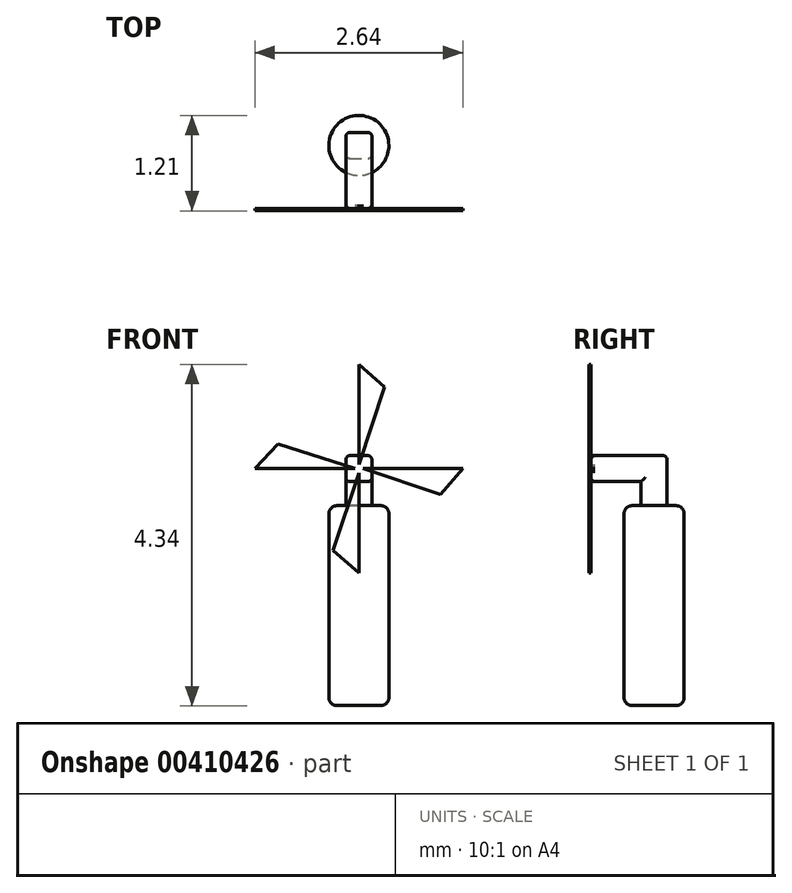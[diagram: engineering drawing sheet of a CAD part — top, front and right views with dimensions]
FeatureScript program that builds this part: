
annotation { "Feature Type Name" : "Feature", "Feature Type Description" : "" }
export const myFeature = defineFeature(function(context is Context, id is Id, definition is map)
    precondition{}
    {
        {
            var Q0;
            Q0=qCreatedBy(makeId("Front.planeOp"),FACE);
            var sketch = newSketch(context, id + "F0", { "sketchPlane" : qUnion([Q0])});
            skLineSegment(sketch, "E0.bottom", {"start": v(0, 1.24) * mm, "end": v(0.38, 1.24) * mm});
            skLineSegment(sketch, "E0.top", {"start": v(0, -1.3) * mm, "end": v(0.38, -1.3) * mm});
            skLineSegment(sketch, "E0.left", {"start": v(0, 1.24) * mm, "end": v(0, -1.3) * mm});
            skLineSegment(sketch, "E0.right", {"start": v(0.38, 1.24) * mm, "end": v(0.38, -1.3) * mm});
            skSolve(sketch);
        }
        {
            var Q0;
            Q0=makeQuery(id+"F0.imprint","IMPRINT",FACE,{"disambiguationData":[TD([[makeQuery(id+"F0.imprint","IMPRINT",EDGE,{"derivedFrom":sQuery(id+"F0.wireOp",EDGE,"E0.bottom")}),-1.0]])]});
            var Q1;
            Q1=sQuery(id+"F0.wireOp",EDGE,"E0.left");
            revolve(context, id + "F1", {"entities" : qUnion([Q0]), "axis" : qUnion([Q1]), "revolveType" : RevolveType.FULL});
        }
        {
            var Q0;
            Q0=makeQuery(id+"F1.opRevolve","SWEPT_FACE",FACE,{"disambiguationData":[OSD([sQuery(id+"F0.wireOp",EDGE,"E0.bottom")])]});
            var sketch = newSketch(context, id + "F2", { "sketchPlane" : qUnion([Q0])});
            skLineSegment(sketch, "E1.bottom", {"start": v(-0.17, 0.17) * mm, "end": v(0.17, 0.17) * mm});
            skLineSegment(sketch, "E1.top", {"start": v(-0.17, -0.17) * mm, "end": v(0.17, -0.17) * mm});
            skLineSegment(sketch, "E1.left", {"start": v(-0.17, 0.17) * mm, "end": v(-0.17, -0.17) * mm});
            skLineSegment(sketch, "E1.right", {"start": v(0.17, 0.17) * mm, "end": v(0.17, -0.17) * mm});
            skPoint(sketch, "E1.middle", {"position": v(0, 0) * mm});
            skSolve(sketch);
        }
        {
            var Q0;
            Q0 = qSketchRegion(id + "F2", true);
            extrude(context, id + "F3", {"entities" : qUnion([Q0]), "operationType" : NewBodyOperationType.ADD, "depth" : 0.64 * mm});
        }
        {
            var Q0;
            Q0=makeQuery(id+"F3.opExtrude","SWEPT_FACE",FACE,{"disambiguationData":[OSD([sQuery(id+"F2.wireOp",EDGE,"E1.top")])]});
            var sketch = newSketch(context, id + "F4", { "sketchPlane" : qUnion([Q0])});
            skLineSegment(sketch, "E2.bottom", {"start": v(-0.17, 1.88) * mm, "end": v(0.17, 1.88) * mm});
            skLineSegment(sketch, "E2.top", {"start": v(-0.17, 1.55) * mm, "end": v(0.17, 1.55) * mm});
            skLineSegment(sketch, "E2.left", {"start": v(-0.17, 1.88) * mm, "end": v(-0.17, 1.55) * mm});
            skLineSegment(sketch, "E2.right", {"start": v(0.17, 1.88) * mm, "end": v(0.17, 1.55) * mm});
            skSolve(sketch);
        }
        {
            var Q0;
            Q0 = qSketchRegion(id + "F4", true);
            extrude(context, id + "F5", {"entities" : qUnion([Q0]), "operationType" : NewBodyOperationType.ADD, "depth" : 0.64 * mm});
        }
        {
            var Q0;
            Q0 = qSketchRegion(id + "F2", true);
            extrude(context, id + "F6", {"entities" : qUnion([Q0]), "operationType" : NewBodyOperationType.ADD, "depth" : 0.64 * mm});
        }
        {
            var Q0;
            Q0=makeQuery(id+"F5.opExtrude","CAP_FACE",FACE,{"disambiguationData":[OSD([sQuery(id+"F4.wireOp",EDGE,"E2.bottom"),sQuery(id+"F4.wireOp",EDGE,"E2.top"),sQuery(id+"F4.wireOp",EDGE,"E2.left"),sQuery(id+"F4.wireOp",EDGE,"E2.right")])],"isStart":false});
            var sketch = newSketch(context, id + "F7", { "sketchPlane" : qUnion([Q0])});
            skPoint(sketch, "E3.startSnap0", {"position": v(-0.17, 1.71) * mm});
            skPoint(sketch, "E3.startSnap1", {"position": v(0, 1.55) * mm});
            skPoint(sketch, "E3.endSnap0", {"position": v(0, 1.88) * mm});
            skPoint(sketch, "E4", {"position": v(0, 1.71) * mm});
            skLineSegment(sketch, "E5", {"start": v(0, 1.77) * mm, "end": v(0, 3.04) * mm});
            skLineSegment(sketch, "E6", {"start": v(0, 3.04) * mm, "end": v(0.33, 2.75) * mm});
            skLineSegment(sketch, "E7", {"start": v(0.33, 2.75) * mm, "end": v(0, 1.77) * mm});
            skSolve(sketch);
        }
        {
            var Q0;
            {var subQ0=sQuery(id+"F7.wireOp",EDGE,"6g4KuSDk-Yey7-5Irt-Qodg-rzQO38CruASS");Q0=makeQuery(id+"F7.imprint","IMPRINT",FACE,{"disambiguationData":[TD([[makeQuery(id+"F7.imprint","IMPRINT",EDGE,{"derivedFrom":subQ0}),-1.0]])]});}
            var Q1;
            {var subQ0=sQuery(id+"F7.wireOp",EDGE,"E6");Q1=makeQuery(id+"F7.imprint","IMPRINT",FACE,{"disambiguationData":[TD([[makeQuery(id+"F7.imprint","IMPRINT",EDGE,{"derivedFrom":subQ0}),-1.0]])]});}
            var Q2;
            {var subQ0=sQuery(id+"F7.wireOp",EDGE,"E7");var subQ1=sQuery(id+"F7.wireOp",EDGE,"E5");var subQ2=makeQuery(id+"F7.imprint","INTERSECT",VERTEX,{"derivedFrom":[subQ1,subQ0]});Q2=makeQuery(id+"F7.imprint","IMPRINT",FACE,{"disambiguationData":[TD([[makeQuery(id+"F7.imprint","IMPRINT",EDGE,{"disambiguationData":[TD([[subQ2,-1.0]])],"derivedFrom":subQ1}),-1.0]])]});}
            extrude(context, id + "F8", {"entities" : qUnion([Q0, Q1, Q2]), "operationType" : NewBodyOperationType.ADD, "depth" : 0.03 * mm});
        }
        {
            var Q0;
            Q0 = qSketchRegion(id + "F7", true);
            extrude(context, id + "F9", {"entities" : qUnion([Q0]), "operationType" : NewBodyOperationType.ADD, "depth" : 0.03 * mm});
        }
        {
            var Q0;
            Q0=makeQuery(id+"F7.imprint","IMPRINT",FACE,{"disambiguationData":[TD([[makeQuery(id+"F7.imprint","IMPRINT",EDGE,{"derivedFrom":makeQuery(id+"F5.opExtrude","CAP_EDGE",EDGE,{"disambiguationData":[OSD([sQuery(id+"F4.wireOp",EDGE,"E2.top")])],"isStart":false})}),1.0]])]});
            var sketch = newSketch(context, id + "F10", { "sketchPlane" : qUnion([Q0])});
            skPoint(sketch, "E8", {"position": v(0, 1.71) * mm});
            skLineSegment(sketch, "E9", {"start": v(0.05, 1.71) * mm, "end": v(1.32, 1.71) * mm});
            skLineSegment(sketch, "E10", {"start": v(1.32, 1.71) * mm, "end": v(1.04, 1.39) * mm});
            skLineSegment(sketch, "E11", {"start": v(1.04, 1.39) * mm, "end": v(0.05, 1.71) * mm});
            skSolve(sketch);
        }
        {
            var Q0;
            Q0 = qSketchRegion(id + "F10", true);
            extrude(context, id + "F11", {"entities" : qUnion([Q0]), "operationType" : NewBodyOperationType.ADD, "depth" : 0.03 * mm});
        }
        {
            var Q0;
            Q0=makeQuery(id+"F7.imprint","IMPRINT",FACE,{"disambiguationData":[TD([[makeQuery(id+"F7.imprint","IMPRINT",EDGE,{"derivedFrom":makeQuery(id+"F5.opExtrude","CAP_EDGE",EDGE,{"disambiguationData":[OSD([sQuery(id+"F4.wireOp",EDGE,"E2.top")])],"isStart":false})}),1.0]])]});
            var sketch = newSketch(context, id + "F12", { "sketchPlane" : qUnion([Q0])});
            skPoint(sketch, "E12", {"position": v(0, 1.71) * mm});
            skLineSegment(sketch, "E13", {"start": v(0, 1.66) * mm, "end": v(0, 0.4) * mm});
            skLineSegment(sketch, "E14", {"start": v(0, 0.4) * mm, "end": v(-0.33, 0.67) * mm});
            skLineSegment(sketch, "E15", {"start": v(-0.33, 0.67) * mm, "end": v(0, 1.66) * mm});
            skSolve(sketch);
        }
        {
            var Q0;
            Q0 = qSketchRegion(id + "F12", true);
            extrude(context, id + "F13", {"entities" : qUnion([Q0]), "operationType" : NewBodyOperationType.ADD, "depth" : 0.03 * mm});
        }
        {
            var Q0;
            Q0=makeQuery(id+"F7.imprint","IMPRINT",FACE,{"disambiguationData":[TD([[makeQuery(id+"F7.imprint","IMPRINT",EDGE,{"derivedFrom":makeQuery(id+"F5.opExtrude","CAP_EDGE",EDGE,{"disambiguationData":[OSD([sQuery(id+"F4.wireOp",EDGE,"E2.top")])],"isStart":false})}),1.0]])]});
            var sketch = newSketch(context, id + "F14", { "sketchPlane" : qUnion([Q0])});
            skPoint(sketch, "E16", {"position": v(0, 1.72) * mm});
            skLineSegment(sketch, "E17", {"start": v(-0.05, 1.72) * mm, "end": v(-1.32, 1.72) * mm});
            skLineSegment(sketch, "E18", {"start": v(-1.32, 1.72) * mm, "end": v(-1.03, 2.03) * mm});
            skLineSegment(sketch, "E19", {"start": v(-1.03, 2.03) * mm, "end": v(-0.05, 1.72) * mm});
            skSolve(sketch);
        }
        {
            var Q0;
            Q0 = qSketchRegion(id + "F14", true);
            extrude(context, id + "F15", {"entities" : qUnion([Q0]), "operationType" : NewBodyOperationType.ADD, "depth" : 0.03 * mm});
        }
        {
            var Q0;
            Q0=makeQuery(id+"F5.boolean.opBoolean","MERGE",EDGE,{"derivedFrom":[makeQuery(id+"F3.opExtrude","CAP_EDGE",EDGE,{"disambiguationData":[OSD([sQuery(id+"F2.wireOp",EDGE,"E1.right")])],"isStart":false}),makeQuery(id+"F5.opExtrude","SWEPT_EDGE",EDGE,{"disambiguationData":[OSD([sQuery(id+"F4.wireOp",EDGE,"E2.bottom"),sQuery(id+"F4.wireOp",EDGE,"E2.right")])]})]});
            var Q1;
            Q1=makeQuery(id+"F5.opExtrude","SWEPT_EDGE",EDGE,{"disambiguationData":[OSD([sQuery(id+"F2.wireOp",EDGE,"E1.top"),sQuery(id+"F2.wireOp",EDGE,"E1.right"),sQuery(id+"F4.wireOp",EDGE,"E2.top"),sQuery(id+"F4.wireOp",EDGE,"E2.right")])]});
            var Q2;
            Q2=makeQuery(id+"F3.opExtrude","SWEPT_EDGE",EDGE,{"disambiguationData":[OSD([sQuery(id+"F2.wireOp",EDGE,"E1.top"),sQuery(id+"F2.wireOp",EDGE,"E1.right")])]});
            var Q3;
            Q3=makeQuery(id+"F3.opExtrude","SWEPT_EDGE",EDGE,{"disambiguationData":[OSD([sQuery(id+"F2.wireOp",EDGE,"E1.bottom"),sQuery(id+"F2.wireOp",EDGE,"E1.right")])]});
            var Q4;
            Q4=makeQuery(id+"F3.opExtrude","SWEPT_EDGE",EDGE,{"disambiguationData":[OSD([sQuery(id+"F2.wireOp",EDGE,"E1.bottom"),sQuery(id+"F2.wireOp",EDGE,"E1.left")])]});
            var Q5;
            Q5=makeQuery(id+"F3.opExtrude","CAP_EDGE",EDGE,{"disambiguationData":[OSD([sQuery(id+"F2.wireOp",EDGE,"E1.bottom")])],"isStart":false});
            var Q6;
            Q6=makeQuery(id+"F5.boolean.opBoolean","MERGE",EDGE,{"derivedFrom":[makeQuery(id+"F3.opExtrude","CAP_EDGE",EDGE,{"disambiguationData":[OSD([sQuery(id+"F2.wireOp",EDGE,"E1.left")])],"isStart":false}),makeQuery(id+"F5.opExtrude","SWEPT_EDGE",EDGE,{"disambiguationData":[OSD([sQuery(id+"F4.wireOp",EDGE,"E2.bottom"),sQuery(id+"F4.wireOp",EDGE,"E2.left")])]})]});
            var Q7;
            Q7=makeQuery(id+"F5.opExtrude","SWEPT_EDGE",EDGE,{"disambiguationData":[OSD([sQuery(id+"F2.wireOp",EDGE,"E1.top"),sQuery(id+"F2.wireOp",EDGE,"E1.left"),sQuery(id+"F4.wireOp",EDGE,"E2.top"),sQuery(id+"F4.wireOp",EDGE,"E2.left")])]});
            var Q8;
            Q8=makeQuery(id+"F3.opExtrude","SWEPT_EDGE",EDGE,{"disambiguationData":[OSD([sQuery(id+"F2.wireOp",EDGE,"E1.top"),sQuery(id+"F2.wireOp",EDGE,"E1.left")])]});
            var Q9;
            {var subQ0=sQuery(id+"F4.wireOp",EDGE,"E2.left");var subQ1=sQuery(id+"F4.wireOp",EDGE,"E2.bottom");var subQ2=makeQuery(id+"F5.opExtrude","CAP_FACE",FACE,{"disambiguationData":[OSD([subQ1,sQuery(id+"F4.wireOp",EDGE,"E2.top"),subQ0,sQuery(id+"F4.wireOp",EDGE,"E2.right")])],"isStart":false});var subQ3=sQuery(id+"F2.wireOp",EDGE,"E1.left");var subQ4=makeQuery(id+"F3.opExtrude","SWEPT_FACE",FACE,{"disambiguationData":[OSD([subQ3])]});var subQ5=makeQuery(id+"F5.opExtrude","SWEPT_FACE",FACE,{"disambiguationData":[OSD([subQ0])]});Q9=makeQuery(id+"F15.boolean.opBoolean","SPLIT",EDGE,{"disambiguationData":[topologyDisambiguationEdgeConnected([subQ4,subQ2,subQ5]),TD([makeQuery(id+"F5.opExtrude","SWEPT_FACE",FACE,{"disambiguationData":[OSD([subQ1])]})])],"derivedFrom":makeQuery(id+"F5.opExtrude","CAP_EDGE",EDGE,{"disambiguationData":[OSD([subQ0])],"isStart":false})});}
            var Q10;
            {var subQ0=sQuery(id+"F4.wireOp",EDGE,"E2.left");var subQ1=makeQuery(id+"F5.opExtrude","SWEPT_FACE",FACE,{"disambiguationData":[OSD([subQ0])]});var subQ2=sQuery(id+"F4.wireOp",EDGE,"E2.top");var subQ3=makeQuery(id+"F5.opExtrude","CAP_FACE",FACE,{"disambiguationData":[OSD([sQuery(id+"F4.wireOp",EDGE,"E2.bottom"),subQ2,subQ0,sQuery(id+"F4.wireOp",EDGE,"E2.right")])],"isStart":false});var subQ4=makeQuery(id+"F3.opExtrude","SWEPT_FACE",FACE,{"disambiguationData":[OSD([sQuery(id+"F2.wireOp",EDGE,"E1.left")])]});Q10=makeQuery(id+"F15.boolean.opBoolean","SPLIT",EDGE,{"disambiguationData":[topologyDisambiguationEdgeConnected([subQ4,subQ3,subQ1]),TD([makeQuery(id+"F5.opExtrude","SWEPT_FACE",FACE,{"disambiguationData":[OSD([subQ2])]})])],"derivedFrom":makeQuery(id+"F5.opExtrude","CAP_EDGE",EDGE,{"disambiguationData":[OSD([subQ0])],"isStart":false})});}
            var Q11;
            {var subQ0=sQuery(id+"F4.wireOp",EDGE,"E2.right");var subQ1=sQuery(id+"F4.wireOp",EDGE,"E2.top");var subQ2=makeQuery(id+"F5.opExtrude","SWEPT_FACE",FACE,{"disambiguationData":[OSD([subQ1])]});var subQ4=makeQuery(id+"F5.opExtrude","CAP_FACE",FACE,{"disambiguationData":[OSD([sQuery(id+"F4.wireOp",EDGE,"E2.bottom"),subQ1,sQuery(id+"F4.wireOp",EDGE,"E2.left"),subQ0])],"isStart":false});Q11=makeQuery(id+"F13.boolean.opBoolean","SPLIT",EDGE,{"disambiguationData":[topologyDisambiguationEdgeConnected([subQ4,subQ2]),TD([makeQuery(id+"F3.opExtrude","SWEPT_FACE",FACE,{"disambiguationData":[OSD([sQuery(id+"F2.wireOp",EDGE,"E1.right")])]})])],"derivedFrom":makeQuery(id+"F5.opExtrude","CAP_EDGE",EDGE,{"disambiguationData":[OSD([subQ1])],"isStart":false})});}
            var Q12;
            {var subQ0=sQuery(id+"F4.wireOp",EDGE,"E2.left");var subQ2=sQuery(id+"F4.wireOp",EDGE,"E2.top");var subQ3=makeQuery(id+"F5.opExtrude","SWEPT_FACE",FACE,{"disambiguationData":[OSD([subQ2])]});var subQ4=makeQuery(id+"F5.opExtrude","CAP_FACE",FACE,{"disambiguationData":[OSD([sQuery(id+"F4.wireOp",EDGE,"E2.bottom"),subQ2,subQ0,sQuery(id+"F4.wireOp",EDGE,"E2.right")])],"isStart":false});Q12=makeQuery(id+"F13.boolean.opBoolean","SPLIT",EDGE,{"disambiguationData":[topologyDisambiguationEdgeConnected([subQ4,subQ3]),TD([makeQuery(id+"F3.opExtrude","SWEPT_FACE",FACE,{"disambiguationData":[OSD([sQuery(id+"F2.wireOp",EDGE,"E1.left")])]})])],"derivedFrom":makeQuery(id+"F5.opExtrude","CAP_EDGE",EDGE,{"disambiguationData":[OSD([subQ2])],"isStart":false})});}
            var Q13;
            {var subQ0=sQuery(id+"F4.wireOp",EDGE,"E2.right");var subQ1=sQuery(id+"F4.wireOp",EDGE,"E2.bottom");var subQ2=makeQuery(id+"F5.opExtrude","CAP_FACE",FACE,{"disambiguationData":[OSD([subQ1,sQuery(id+"F4.wireOp",EDGE,"E2.top"),sQuery(id+"F4.wireOp",EDGE,"E2.left"),subQ0])],"isStart":false});var subQ3=sQuery(id+"F2.wireOp",EDGE,"E1.right");var subQ4=makeQuery(id+"F3.opExtrude","SWEPT_FACE",FACE,{"disambiguationData":[OSD([subQ3])]});var subQ5=makeQuery(id+"F5.opExtrude","SWEPT_FACE",FACE,{"disambiguationData":[OSD([subQ0])]});Q13=makeQuery(id+"F11.boolean.opBoolean","SPLIT",EDGE,{"disambiguationData":[topologyDisambiguationEdgeConnected([subQ4,subQ2,subQ5]),TD([makeQuery(id+"F5.opExtrude","SWEPT_FACE",FACE,{"disambiguationData":[OSD([subQ1])]})])],"derivedFrom":makeQuery(id+"F5.opExtrude","CAP_EDGE",EDGE,{"disambiguationData":[OSD([subQ0])],"isStart":false})});}
            var Q14;
            {var subQ0=sQuery(id+"F4.wireOp",EDGE,"E2.right");var subQ1=makeQuery(id+"F5.opExtrude","SWEPT_FACE",FACE,{"disambiguationData":[OSD([subQ0])]});var subQ2=sQuery(id+"F4.wireOp",EDGE,"E2.top");var subQ3=makeQuery(id+"F5.opExtrude","CAP_FACE",FACE,{"disambiguationData":[OSD([sQuery(id+"F4.wireOp",EDGE,"E2.bottom"),subQ2,sQuery(id+"F4.wireOp",EDGE,"E2.left"),subQ0])],"isStart":false});var subQ5=makeQuery(id+"F3.opExtrude","SWEPT_FACE",FACE,{"disambiguationData":[OSD([sQuery(id+"F2.wireOp",EDGE,"E1.right")])]});Q14=makeQuery(id+"F11.boolean.opBoolean","SPLIT",EDGE,{"disambiguationData":[topologyDisambiguationEdgeConnected([subQ5,subQ3,subQ1]),TD([makeQuery(id+"F5.opExtrude","SWEPT_FACE",FACE,{"disambiguationData":[OSD([subQ2])]})])],"derivedFrom":makeQuery(id+"F5.opExtrude","CAP_EDGE",EDGE,{"disambiguationData":[OSD([subQ0])],"isStart":false})});}
            var Q15;
            {var subQ0=sQuery(id+"F4.wireOp",EDGE,"E2.right");var subQ1=sQuery(id+"F4.wireOp",EDGE,"E2.bottom");var subQ2=makeQuery(id+"F5.opExtrude","CAP_FACE",FACE,{"disambiguationData":[OSD([subQ1,sQuery(id+"F4.wireOp",EDGE,"E2.top"),sQuery(id+"F4.wireOp",EDGE,"E2.left"),subQ0])],"isStart":false});var subQ3=makeQuery(id+"F5.opExtrude","SWEPT_FACE",FACE,{"disambiguationData":[OSD([subQ1])]});var subQ4=sQuery(id+"F2.wireOp",EDGE,"E1.right");var subQ6=makeQuery(id+"F3.opExtrude","CAP_FACE",FACE,{"disambiguationData":[OSD([sQuery(id+"F2.wireOp",EDGE,"E1.bottom"),sQuery(id+"F2.wireOp",EDGE,"E1.top"),sQuery(id+"F2.wireOp",EDGE,"E1.left"),subQ4])],"isStart":false});Q15=makeQuery(id+"F8.boolean.opBoolean","SPLIT",EDGE,{"disambiguationData":[topologyDisambiguationEdgeConnected([subQ6,subQ3,subQ2]),TD([makeQuery(id+"F3.opExtrude","SWEPT_FACE",FACE,{"disambiguationData":[OSD([subQ4])]})])],"derivedFrom":makeQuery(id+"F5.opExtrude","CAP_EDGE",EDGE,{"disambiguationData":[OSD([subQ1])],"isStart":false})});}
            fillet(context, id + "F16", {"entities" : qUnion([Q0, Q1, Q2, Q3, Q4, Q5, Q6, Q7, Q8, Q9, Q10, Q11, Q12, Q13, Q14, Q15]), "radius" : 0.05 * mm, "tangentPropagation" : true, "allowEdgeOverflow" : false});
        }
        {
            var Q0;
            Q0=makeQuery(id+"F1.opRevolve","SWEPT_EDGE",EDGE,{"disambiguationData":[OSD([sQuery(id+"F0.wireOp",EDGE,"E0.bottom"),sQuery(id+"F0.wireOp",EDGE,"E0.right")])]});
            var Q1;
            Q1=makeQuery(id+"F1.opRevolve","SWEPT_EDGE",EDGE,{"disambiguationData":[OSD([sQuery(id+"F0.wireOp",EDGE,"E0.top"),sQuery(id+"F0.wireOp",EDGE,"E0.right")])]});
            fillet(context, id + "F17", {"entities" : qUnion([Q0, Q1]), "radius" : 0.1 * mm, "tangentPropagation" : true, "allowEdgeOverflow" : false});
        }
    });
